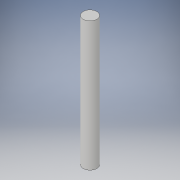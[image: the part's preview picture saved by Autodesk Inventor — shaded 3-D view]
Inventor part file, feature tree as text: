
AUTODESK INVENTOR PART (.ipt)
format: ipt  version: 2019 (Build 230136000, 136)  size: 89,600 bytes
history: native  units: mm
features: extrude x1, sketch x1
ambient origin geometry x8: Origin, YZ Plane, XZ Plane, XY Plane, X Axis, Y Axis, Z Axis, Center Point
bodies: Solid1 (feature_tree)
feature tree (2):
  extrude  "Extrusion1"  Depth=76.0mm TaperAngle=0.0deg
  sketch  "Sketch1"  dims[d0=8.0mm d1=76.0mm d2=0.0mm]
